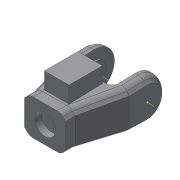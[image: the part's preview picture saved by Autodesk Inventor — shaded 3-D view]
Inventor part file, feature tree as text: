
AUTODESK INVENTOR PART (.ipt)
format: ipt  version: 2018 (Build 220112000, 112)  size: 860,160 bytes
history: native  units: mm
features: sketch x46, projected_geometry x43, extrude x41, other x10, chamfer x6, fillet x5, hole x3, reference x3, mirror x1, plane x1, imported_body x1, boolean_combine x1
ambient origin geometry x8: Origin, YZ Plane, XZ Plane, XY Plane, X Axis, Y Axis, Z Axis, Center Point
bodies: Solid1 (feature_tree), Solid2 (feature_tree)
feature tree (161):
  extrude  "Extrusion1"  Depth=45.0mm
  extrude  "Extrusion2"  Depth=2.25mm
  hole  "Hole1"  [1 undecoded]
  hole  "Hole2"  [1 undecoded]
  fillet  "Fillet1"  Radius=14.0mm
  extrude  "Extrusion3"  Depth=5.25mm
  extrude  "Extrusion4"  Depth=10.0mm
  extrude  "Extrusion5"  Depth=2.195mm
  extrude  "Extrusion6"  Depth=8.0mm
  hole  "Hole3"  [1 undecoded]
  extrude  "Extrusion7"  Depth=8.0mm
  extrude  "Extrusion8"  Depth=1.0mm TaperAngle=0.0deg
  extrude  "Extrusion9"  Depth=24.5mm
  extrude  "Extrusion10"  Depth=10.0mm
  extrude  "Extrusion11"  Depth=14.5mm
  extrude  "Extrusion13"  Depth=20.0mm
  extrude  "Extrusion14"  Depth=5.0mm
  extrude  "Extrusion15"  Depth=2.25mm
  extrude  "Extrusion16"  Depth=5.0mm
  extrude  "Extrusion17"  Depth=9.0mm
  chamfer  "Chamfer1"  Distance=1.0mm
  fillet  "Fillet7"  Radius=20.7mm
  fillet  "Fillet8"  Radius=32.0mm
  mirror  "Mirror1"
  sketch  "Sketch26"  dims[d55=2.25mm d56=5.0mm]
  extrude  "Extrusion24"  Depth=1.0mm TaperAngle=0.0deg
  extrude  "Extrusion25"  Depth=8.0mm
  extrude  "Extrusion26"  Depth=0.2mm TaperAngle=0.0deg
  extrude  "Extrusion27"  Depth=8.0mm TaperAngle=0.0deg
  other  "Work Axis1"
  plane  "Work Plane2"
  extrude  "Extrusion28"  Depth=0.2mm TaperAngle=0.0deg
  extrude  "Extrusion29"  Depth=2.5mm TaperAngle=45.0deg
  extrude  "Extrusion31"  Depth=0.5mm
  extrude  "Extrusion32"  Depth=36.0mm
  extrude  "Extrusion33"  Depth=60.0mm
  sketch  "Sketch41"  dims[d100=0.2mm d101=0.0mm d102=2.5mm d103=2.0mm d104=45.0deg]
  extrude  "Extrusion34"  Depth=2.3mm
  chamfer  "Chamfer6"  Distance=15.0mm
  fillet  "Fillet9"  Radius=15.0mm
  extrude  "Extrusion35"  Depth=15.0mm TaperAngle=0.0deg
  extrude  "Extrusion36"  Depth=41.5mm
  fillet  "Fillet10"  Radius=15.5mm
  extrude  "Extrusion37"  Depth=5.0mm
  extrude  "Extrusion38"  Depth=100.0mm TaperAngle=0.0deg
  extrude  "Extrusion40"  Depth=11.5mm
  extrude  "Extrusion41"  Depth=11.5mm
  extrude  "Extrusion42"  Depth=7.0mm
  chamfer  "Chamfer10"  Distance=100.0mm
  chamfer  "Chamfer11"  Distance=100.0mm
  chamfer  "Chamfer12"  Distance=100.0mm
  chamfer  "Chamfer13"  Distance=5.0mm Angle=45.0deg
  sketch  "Sketch61"  dims[d172=0.0mm d173=11.5mm]
  sketch  "Sketch62"  dims[d175=11.5mm d176=11.5mm]
  extrude  "Extrusion47"  TaperAngle=15.0deg  [1 undecoded]
  extrude  "Extrusion48"  Depth=15.470628mm
  extrude  "Extrusion49"  Depth=1.0mm TaperAngle=0.0deg
  extrude  "Extrusion50"  TaperAngle=15.0deg  [1 undecoded]
  extrude  "Extrusion51"  Depth=10.0mm
  extrude  "Extrusion52"  Depth=10.0mm TaperAngle=0.0deg
  extrude  "Extrusion53"  Depth=10.0mm
  extrude  "Extrusion54"  Depth=10.0mm TaperAngle=0.0deg
  imported_body  "Base1"
  boolean_combine  "Combine1"
  sketch  "Sketch1"  dims[d0=24.5mm d1=45.0mm]
  sketch  "Sketch2"  dims[d2=1.95mm d3=0.0mm d4=2.25mm]
  projected_geometry  "Projected Loop1"
  sketch  "Sketch3"  dims[d5=20.0mm d6=2.25mm]
  projected_geometry  "Projected Loop2"
  sketch  "Sketch4"  dims[d7=5.25mm d8=5.25mm d9=14.0mm]
  projected_geometry  "Projected Loop3"
  sketch  "Sketch5"  dims[d10=5.25mm d11=18.5mm]
  projected_geometry  "Projected Loop4"
  sketch  "Sketch6"  dims[d12=10.0mm d13=0.0mm d14=20.5mm]
  projected_geometry  "Projected Loop5"
  sketch  "Sketch7"  dims[d15=2.0mm d16=2.195mm]
  projected_geometry  "Projected Loop6"
  sketch  "Sketch8"  dims[d17=2.0mm]
  projected_geometry  "Projected Loop7"
  sketch  "Sketch9"  dims[d18=2.4mm d19=6.0mm d20=4.4mm d21=2.0mm d22=90.0deg d23=8.0mm d24=20.594885mm d25=20.5mm]
  projected_geometry  "Projected Loop8"
  projected_geometry  "Projected Loop9"
  sketch  "Sketch10"  dims[d26=26.65mm d27=2.0mm]
  projected_geometry  "Projected Loop10"
  projected_geometry  "Projected Loop11"
  sketch  "Sketch11"  dims[d28=2.0mm]
  projected_geometry  "Projected Loop12"
  sketch  "Sketch12"  dims[d29=2.4mm d30=6.0mm d31=4.4mm d32=2.0mm d33=90.0deg d34=8.0mm d35=20.594885mm d36=0.5mm]
  sketch  "Sketch13"  dims[d37=18.0mm d38=1.0mm d39=0.0mm]
  sketch  "Sketch14"  dims[d41=5.0mm d42=0.0mm d43=24.5mm]
  projected_geometry  "Projected Loop13"
  sketch  "Sketch16"  dims[d44=1.15mm d45=0.0mm d46=10.0mm]
  projected_geometry  "Projected Loop14"
  sketch  "Sketch17"  dims[d47=21.0mm d48=14.5mm]
  projected_geometry  "Projected Loop15"
  sketch  "Sketch18"  dims[d49=20.0mm d50=14.5mm]
  projected_geometry  "Projected Loop16"
  sketch  "Sketch19"  dims[d51=24.5mm d52=5.0mm]
  projected_geometry  "Projected Loop17"
  sketch  "Sketch20"  dims[d53=5.0mm d54=2.25mm]
  projected_geometry  "Projected Loop18"
  projected_geometry  "Projected Loop25"
  sketch  "Sketch31"  dims[d57=5.0mm d58=9.0mm]
  projected_geometry  "Projected Loop30"
  reference  "Reference1"
  sketch  "Sketch32"  dims[d59=14.75mm]
  projected_geometry  "Projected Loop31"
  sketch  "Sketch33"  dims[d60=4.0mm d61=1.0mm d62=0.0mm d63=20.7mm]
  projected_geometry  "Projected Loop32"
  sketch  "Sketch34"  dims[d64=2.3mm d65=6.0mm d66=4.4mm d67=2.0mm d68=90.0deg d69=8.0mm d70=20.594885mm d72=32.0mm]
  projected_geometry  "Projected Loop33"
  other  "Work Point1"
  other  "Work Point2"
  other  "Work Point3"
  sketch  "Sketch35"  dims[d73=3.0mm d74=0.0mm d75=1.0mm d76=0.0mm]
  sketch  "Sketch37"  dims[d77=12.25mm d78=0.0mm d80=8.0mm]
  projected_geometry  "Projected Loop34"
  sketch  "Sketch38"  dims[d81=4.5mm d82=0.0mm d84=0.2mm d85=0.0mm]
  sketch  "Sketch39"  dims[d91=8.0mm d92=0.0mm d93=5.0mm d94=0.0mm]
  sketch  "Sketch40"  dims[d95=5.0mm d96=0.0mm d98=0.2mm d99=0.0mm]
  projected_geometry  "Projected Loop35"
  projected_geometry  "Projected Loop36"
  projected_geometry  "Projected Loop37"
  projected_geometry  "Projected Loop38"
  sketch  "Sketch42"  dims[d105=1.5mm d114=0.5mm]
  projected_geometry  "Projected Loop39"
  sketch  "Sketch43"  dims[d130=60.0mm d131=36.0mm]
  reference  "Reference2"
  reference  "Reference3"
  sketch  "Sketch45"  dims[d146=40.0mm d147=60.0mm]
  projected_geometry  "Projected Loop40"
  sketch  "Sketch46"  dims[d148=0.0mm d149=2.3mm d150=15.0mm d151=0.0mm d152=15.0mm d153=0.0mm]
  projected_geometry  "Projected Loop41"
  sketch  "Sketch48"  dims[d154=15.0mm d155=0.0mm d156=15.0mm d157=0.0mm]
  projected_geometry  "Projected Loop43"
  sketch  "Sketch50"  dims[d158=20.5mm d159=41.5mm d160=15.5mm]
  projected_geometry  "Projected Loop46"
  sketch  "Sketch53"  dims[d161=15.5mm d162=5.0mm]
  projected_geometry  "Projected Loop47"
  sketch  "Sketch55"  dims[d165=100.0mm d166=0.0mm d167=100.0mm d168=0.0mm]
  projected_geometry  "Projected Loop60"
  sketch  "Sketch63"  dims[d179=100.0mm d180=0.0mm d187=7.0mm d188=100.0mm d189=0.0mm d193=100.0mm d194=0.0mm d195=100.0mm d196=0.0mm d197=5.0mm d198=2.0mm d199=45.0deg]
  projected_geometry  "Projected Loop61"
  sketch  "Sketch64"  dims[d200=8.0mm d202=15.0deg]
  projected_geometry  "Projected Loop62"
  sketch  "Sketch65"  dims[d204=10.970628mm d205=15.470628mm]
  projected_geometry  "Projected Loop63"
  sketch  "Sketch66"  dims[d206=1.0mm d207=0.0mm d208=1.0mm d209=0.0mm]
  projected_geometry  "Projected Loop64"
  sketch  "Sketch67"  dims[d213=2.0mm d215=15.0deg]
  projected_geometry  "Projected Loop65"
  sketch  "Sketch68"  dims[d216=4.0mm d217=4.0mm d218=5.0mm d219=0.0mm d222=32.0mm d223=4.0mm d224=0.0mm d227=6.5mm d228=0.0mm d244=20.5mm d245=3.05mm d246=0.0mm d255=20.5mm d256=1.55mm d257=0.0mm d330=3.0mm d331=2.0mm d332=45.0deg d333=4.5mm d334=20.0mm d335=45.0deg d336=5.0mm d337=20.0mm d338=45.0deg d339=5.0mm d340=20.0mm d341=45.0deg d361=10.0mm d362=0.0mm d363=2.0mm d364=51.5mm d365=0.0mm d366=45.0mm d367=0.0mm d368=3.0mm d369=0.0mm d370=51.5mm d371=0.0mm d372=51.5mm d373=0.0mm d374=51.5mm d375=0.0mm d376=51.5mm d377=0.0mm d378=51.5mm d379=0.0mm]
  projected_geometry  "Projected Loop66"
  parser-record x1  (decoder bookkeeping rows leaked as tree rows — omitted from the tree; the rows remain in map.json)
  other  "servocheck.iam"
  other  "LX-16A:3"
  other  "DUOPAN-SG-SJ_10"
  projected_geometry  "Project Cut Edges1"
  projected_geometry  "Project Cut Edges3"
  other  "bottomarm:1"
  other  "arm1:1"
note: 5 required parameter values undecoded (feature->parameter linkage not recoverable at this tier; creation-order binding heuristic only, values carry confidence <= 0.55)
note: 1 file-system path scrubbed to <path> (originals preserved in map.json)
